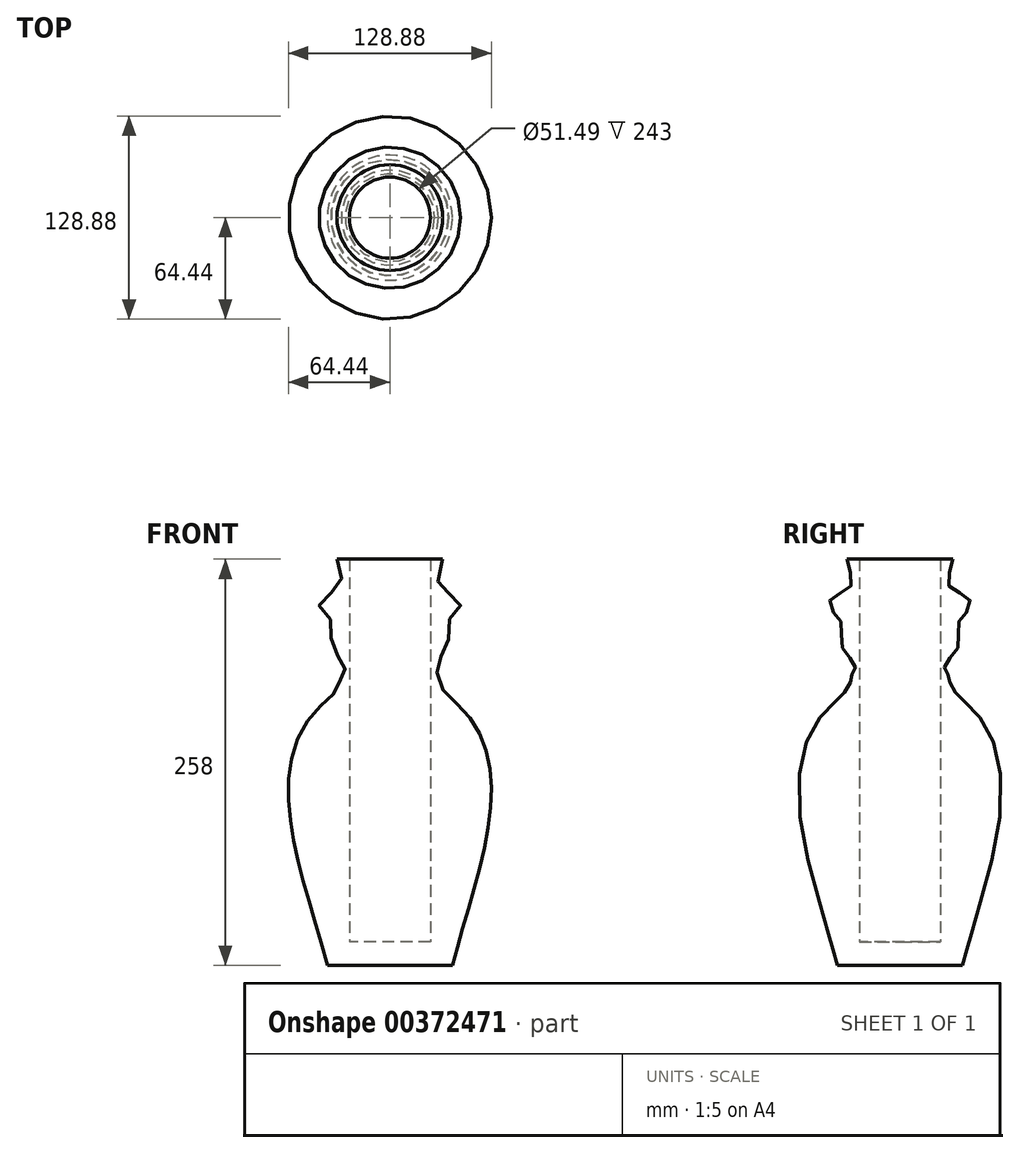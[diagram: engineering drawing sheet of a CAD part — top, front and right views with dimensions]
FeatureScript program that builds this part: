
annotation { "Feature Type Name" : "Feature", "Feature Type Description" : "" }
export const myFeature = defineFeature(function(context is Context, id is Id, definition is map)
    precondition{}
    {
        {
            var Q0;
            Q0=qCreatedBy(makeId("Top.planeOp"),FACE);
            var sketch = newSketch(context, id + "F0", { "sketchPlane" : qUnion([Q0])});
            skCircle(sketch, "E0", {"center": v(0, 0) * mm, "radius": 39.72 * mm});
            skSolve(sketch);
        }
        {
            var Q0;
            Q0=qCreatedBy(makeId("Top.planeOp"),FACE);
            cPlane(context, id + "F1", {"entities" : qUnion([Q0]), "cplaneType" : CPlaneType.OFFSET, "offset" : 15 * mm, "width" : 150 * mm, "height" : 150 * mm});
        }
        {
            var Q0;
            Q0=qCreatedBy(id+"F1.planeOp",FACE);
            var sketch = newSketch(context, id + "F2", { "sketchPlane" : qUnion([Q0])});
            skCircle(sketch, "E1", {"center": v(0, 0) * mm, "radius": 43.83 * mm});
            skSolve(sketch);
        }
        {
            var Q0;
            Q0=qCreatedBy(id+"F1.planeOp",FACE);
            cPlane(context, id + "F3", {"entities" : qUnion([Q0]), "cplaneType" : CPlaneType.OFFSET, "offset" : 150 * mm, "width" : 150 * mm, "height" : 150 * mm});
        }
        {
            var Q0;
            Q0=qCreatedBy(id+"F3.planeOp",FACE);
            var sketch = newSketch(context, id + "F4", { "sketchPlane" : qUnion([Q0])});
            skCircle(sketch, "E2", {"center": v(0, 0) * mm, "radius": 43.81 * mm});
            skSolve(sketch);
        }
        {
            var Q0;
            Q0=qCreatedBy(id+"F3.planeOp",FACE);
            cPlane(context, id + "F5", {"entities" : qUnion([Q0]), "cplaneType" : CPlaneType.OFFSET, "offset" : 15 * mm, "width" : 150 * mm, "height" : 150 * mm});
        }
        {
            var Q0;
            Q0=qCreatedBy(id+"F5.planeOp",FACE);
            var sketch = newSketch(context, id + "F6", { "sketchPlane" : qUnion([Q0])});
            skCircle(sketch, "E3", {"center": v(0, 0) * mm, "radius": 31.54 * mm});
            skSolve(sketch);
        }
        {
            var Q0;
            Q0=qCreatedBy(id+"F5.planeOp",FACE);
            cPlane(context, id + "F7", {"entities" : qUnion([Q0]), "cplaneType" : CPlaneType.OFFSET, "offset" : 3 * mm, "width" : 150 * mm, "height" : 150 * mm});
        }
        {
            var Q0;
            Q0=qCreatedBy(id+"F7.planeOp",FACE);
            cPlane(context, id + "F8", {"entities" : qUnion([Q0]), "cplaneType" : CPlaneType.OFFSET, "offset" : 3 * mm, "width" : 150 * mm, "height" : 150 * mm});
        }
        {
            var Q0;
            Q0=qCreatedBy(id+"F8.planeOp",FACE);
            cPlane(context, id + "F9", {"entities" : qUnion([Q0]), "cplaneType" : CPlaneType.OFFSET, "offset" : 3 * mm, "width" : 150 * mm, "height" : 150 * mm});
        }
        {
            var Q0;
            Q0=qCreatedBy(id+"F9.planeOp",FACE);
            cPlane(context, id + "F10", {"entities" : qUnion([Q0]), "cplaneType" : CPlaneType.OFFSET, "offset" : 3 * mm, "width" : 150 * mm, "height" : 150 * mm});
        }
        {
            var Q0;
            Q0=qCreatedBy(id+"F10.planeOp",FACE);
            cPlane(context, id + "F11", {"entities" : qUnion([Q0]), "cplaneType" : CPlaneType.OFFSET, "offset" : 3 * mm, "width" : 150 * mm, "height" : 150 * mm});
        }
        {
            var Q0;
            Q0=qCreatedBy(id+"F8.planeOp",FACE);
            var sketch = newSketch(context, id + "F12", { "sketchPlane" : qUnion([Q0])});
            skCircle(sketch, "E4", {"center": v(0, 0) * mm, "radius": 29.95 * mm});
            skSolve(sketch);
        }
        {
            var Q0;
            Q0=qCreatedBy(id+"F9.planeOp",FACE);
            var sketch = newSketch(context, id + "F13", { "sketchPlane" : qUnion([Q0])});
            skCircle(sketch, "E5", {"center": v(0, 0) * mm, "radius": 28.18 * mm});
            skSolve(sketch);
        }
        {
            var Q0;
            Q0=qCreatedBy(id+"F10.planeOp",FACE);
            var sketch = newSketch(context, id + "F14", { "sketchPlane" : qUnion([Q0])});
            skCircle(sketch, "E6", {"center": v(0, 0) * mm, "radius": 30.22 * mm});
            skSolve(sketch);
        }
        {
            var Q0;
            Q0=qCreatedBy(id+"F11.planeOp",FACE);
            var sketch = newSketch(context, id + "F15", { "sketchPlane" : qUnion([Q0])});
            skCircle(sketch, "E7", {"center": v(0, 0) * mm, "radius": 31.52 * mm});
            skSolve(sketch);
        }
        {
            var Q0;
            Q0=qCreatedBy(id+"F11.planeOp",FACE);
            cPlane(context, id + "F16", {"entities" : qUnion([Q0]), "cplaneType" : CPlaneType.OFFSET, "offset" : 3 * mm, "width" : 150 * mm, "height" : 150 * mm});
        }
        {
            var Q0;
            Q0=qCreatedBy(id+"F16.planeOp",FACE);
            var sketch = newSketch(context, id + "F17", { "sketchPlane" : qUnion([Q0])});
            skCircle(sketch, "E8", {"center": v(0, 0) * mm, "radius": 34.65 * mm});
            skSolve(sketch);
        }
        {
            var Q0;
            Q0=qCreatedBy(id+"F16.planeOp",FACE);
            cPlane(context, id + "F18", {"entities" : qUnion([Q0]), "cplaneType" : CPlaneType.OFFSET, "offset" : 25 * mm, "width" : 150 * mm, "height" : 150 * mm});
        }
        {
            var Q0;
            Q0=qCreatedBy(id+"F18.planeOp",FACE);
            var sketch = newSketch(context, id + "F19", { "sketchPlane" : qUnion([Q0])});
            skCircle(sketch, "E9", {"center": v(0, 0) * mm, "radius": 40.21 * mm});
            skSolve(sketch);
        }
        {
            var Q0;
            Q0=qCreatedBy(id+"F18.planeOp",FACE);
            cPlane(context, id + "F20", {"entities" : qUnion([Q0]), "cplaneType" : CPlaneType.OFFSET, "offset" : 2 * mm, "width" : 150 * mm, "height" : 150 * mm});
        }
        {
            var Q0;
            Q0=qCreatedBy(id+"F20.planeOp",FACE);
            var sketch = newSketch(context, id + "F21", { "sketchPlane" : qUnion([Q0])});
            skCircle(sketch, "E10", {"center": v(0, 0) * mm, "radius": 43.5 * mm});
            skSolve(sketch);
        }
        {
            var Q0;
            Q0=qCreatedBy(id+"F20.planeOp",FACE);
            cPlane(context, id + "F22", {"entities" : qUnion([Q0]), "cplaneType" : CPlaneType.OFFSET, "offset" : 9 * mm, "width" : 150 * mm, "height" : 150 * mm});
        }
        {
            var Q0;
            Q0=qCreatedBy(id+"F22.planeOp",FACE);
            var sketch = newSketch(context, id + "F23", { "sketchPlane" : qUnion([Q0])});
            skCircle(sketch, "E11", {"center": v(0, 0) * mm, "radius": 43.22 * mm});
            skSolve(sketch);
        }
        {
            var Q0;
            Q0=qCreatedBy(id+"F22.planeOp",FACE);
            cPlane(context, id + "F24", {"entities" : qUnion([Q0]), "cplaneType" : CPlaneType.OFFSET, "offset" : 4 * mm, "width" : 150 * mm, "height" : 150 * mm});
        }
        {
            var Q0;
            Q0=qCreatedBy(id+"F24.planeOp",FACE);
            var sketch = newSketch(context, id + "F25", { "sketchPlane" : qUnion([Q0])});
            skCircle(sketch, "E12", {"center": v(0, 0) * mm, "radius": 33.43 * mm});
            skSolve(sketch);
        }
        {
            var Q0;
            Q0=qCreatedBy(id+"F24.planeOp",FACE);
            cPlane(context, id + "F26", {"entities" : qUnion([Q0]), "cplaneType" : CPlaneType.OFFSET, "offset" : 20 * mm, "width" : 150 * mm, "height" : 150 * mm});
        }
        {
            var Q0;
            Q0=qCreatedBy(id+"F26.planeOp",FACE);
            var sketch = newSketch(context, id + "F27", { "sketchPlane" : qUnion([Q0])});
            skCircle(sketch, "E13", {"center": v(0, 0) * mm, "radius": 33.57 * mm});
            skSolve(sketch);
        }
        {
            var Q0;
            Q0 = qSketchRegion(id + "F0", true);
            var Q1;
            Q1 = qSketchRegion(id + "F2", true);
            var Q2;
            Q2 = qSketchRegion(id + "F4", true);
            var Q3;
            Q3 = qSketchRegion(id + "F6", true);
            var Q4;
            Q4 = qSketchRegion(id + "F12", true);
            var Q5;
            Q5 = qSketchRegion(id + "F13", true);
            var Q6;
            Q6 = qSketchRegion(id + "F14", true);
            var Q7;
            Q7 = qSketchRegion(id + "F15", true);
            var Q8;
            Q8 = qSketchRegion(id + "F17", true);
            var Q9;
            Q9 = qSketchRegion(id + "F19", true);
            var Q10;
            Q10 = qSketchRegion(id + "F21", true);
            var Q11;
            Q11 = qSketchRegion(id + "F23", true);
            var Q12;
            Q12 = qSketchRegion(id + "F25", true);
            var Q13;
            Q13 = qSketchRegion(id + "F27", true);
            loft(context, id + "F28", {"sheetProfilesArray" : [{ "sheetProfileEntities" : qUnion([Q0]) }, { "sheetProfileEntities" : qUnion([Q1]) }, { "sheetProfileEntities" : qUnion([Q2]) }, { "sheetProfileEntities" : qUnion([Q3]) }, { "sheetProfileEntities" : qUnion([Q4]) }, { "sheetProfileEntities" : qUnion([Q5]) }, { "sheetProfileEntities" : qUnion([Q6]) }, { "sheetProfileEntities" : qUnion([Q7]) }, { "sheetProfileEntities" : qUnion([Q8]) }, { "sheetProfileEntities" : qUnion([Q9]) }, { "sheetProfileEntities" : qUnion([Q10]) }, { "sheetProfileEntities" : qUnion([Q11]) }, { "sheetProfileEntities" : qUnion([Q12]) }, { "sheetProfileEntities" : qUnion([Q13]) }]});
        }
        {
            var Q0;
            Q0=qCreatedBy(id+"F1.planeOp",FACE);
            var sketch = newSketch(context, id + "F29", { "sketchPlane" : qUnion([Q0])});
            skCircle(sketch, "E14", {"center": v(0, 0) * mm, "radius": 25.75 * mm});
            skSolve(sketch);
        }
        {
            var Q0;
            Q0 = qSketchRegion(id + "F29", true);
            extrude(context, id + "F30", {"entities" : qUnion([Q0]), "operationType" : NewBodyOperationType.REMOVE, "depth" : 271 * mm});
        }
    });
